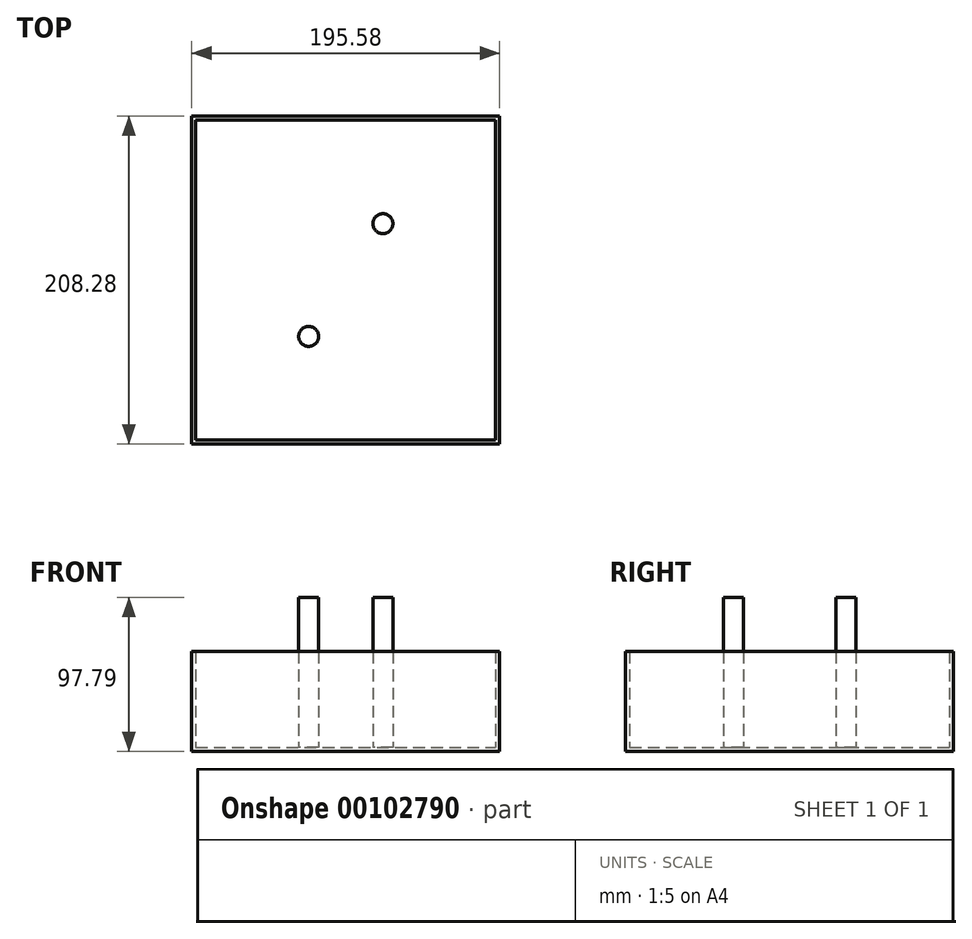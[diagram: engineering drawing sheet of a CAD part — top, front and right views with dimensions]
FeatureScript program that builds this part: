
annotation { "Feature Type Name" : "Feature", "Feature Type Description" : "" }
export const myFeature = defineFeature(function(context is Context, id is Id, definition is map)
    precondition{}
    {
        {
            var Q0;
            Q0=qCreatedBy(makeId("Top.planeOp"),FACE);
            var sketch = newSketch(context, id + "F0", { "sketchPlane" : qUnion([Q0])});
            skLineSegment(sketch, "E0", {"start": v(0, 0) * mm, "end": v(0, 104.14) * mm});
            skLineSegment(sketch, "E1", {"start": v(0, 104.14) * mm, "end": v(97.8, 104.14) * mm});
            skLineSegment(sketch, "E2", {"start": v(97.8, 104.14) * mm, "end": v(97.8, 0) * mm});
            skLineSegment(sketch, "E3.MirrorCS", {"start": v(0, 104.14) * mm, "end": v(-97.8, 104.14) * mm});
            skLineSegment(sketch, "E4.MirrorCS", {"start": v(97.8, -104.14) * mm, "end": v(97.79, 0) * mm});
            skLineSegment(sketch, "E5", {"start": v(-97.8, -104.14) * mm, "end": v(97.8, -104.14) * mm});
            skLineSegment(sketch, "E6", {"start": v(-97.8, -104.14) * mm, "end": v(-97.8, 104.14) * mm});
            skSolve(sketch);
        }
        {
            var Q0;
            Q0 = qSketchRegion(id + "F0", true);
            extrude(context, id + "F1", {"entities" : qUnion([Q0]), "depth" : 63.5 * mm});
        }
        {
            var Q0;
            Q0=makeQuery(id+"F1.opExtrude","CAP_FACE",FACE,{"disambiguationData":[OSD([sQuery(id+"F0.wireOp",EDGE,"E1"),sQuery(id+"F0.wireOp",EDGE,"E2"),sQuery(id+"F0.wireOp",EDGE,"8faf7771-bb4b-4e78-9b49-a767b9c531a00.MirrorCS"),sQuery(id+"F0.wireOp",EDGE,"E3.MirrorCS"),sQuery(id+"F0.wireOp",EDGE,"8fe53615-c728-4495-bf62-b4da586d37250.MirrorCS"),sQuery(id+"F0.wireOp",EDGE,"b9aa1892-de12-408e-bb1e-22edbf4f4b020.MirrorCS"),sQuery(id+"F0.wireOp",EDGE,"4fff83c6-06de-462e-9df9-fc56c3a055500.MirrorCS"),sQuery(id+"F0.wireOp",EDGE,"E4.MirrorCS")])],"isStart":false});
            shell(context, id + "F2", {"entities" : qUnion([Q0]), "thickness" : 2.54 * mm});
        }
        {
            var Q0;
            Q0=makeQuery(id+"F2.opShell","OFFSET_FACE",FACE,{"disambiguationData":[OSD([sQuery(id+"F0.wireOp",EDGE,"E1"),sQuery(id+"F0.wireOp",EDGE,"E2"),sQuery(id+"F0.wireOp",EDGE,"E3.MirrorCS"),sQuery(id+"F0.wireOp",EDGE,"E4.MirrorCS"),sQuery(id+"F0.wireOp",EDGE,"E5"),sQuery(id+"F0.wireOp",EDGE,"E6")])]});
            var sketch = newSketch(context, id + "F3", { "sketchPlane" : qUnion([Q0])});
            skCircle(sketch, "E7", {"center": v(-23.58, -35.83) * mm, "radius": 50.8 * mm});
            skCircle(sketch, "E8", {"center": v(23.58, 35.83) * mm, "radius": 34.3 * mm});
            skCircle(sketch, "E9", {"center": v(-23.58, -35.83) * mm, "radius": 6.35 * mm});
            skCircle(sketch, "E10", {"center": v(23.58, 35.83) * mm, "radius": 6.35 * mm});
            skSolve(sketch);
        }
        {
            var Q0;
            Q0=makeQuery(id+"F3.imprint","IMPRINT",FACE,{"disambiguationData":[TD([[makeQuery(id+"F3.imprint","IMPRINT",EDGE,{"derivedFrom":sQuery(id+"F3.wireOp",EDGE,"E10")}),1.0]])]});
            var Q1;
            Q1=makeQuery(id+"F3.imprint","IMPRINT",FACE,{"disambiguationData":[TD([[makeQuery(id+"F3.imprint","IMPRINT",EDGE,{"derivedFrom":sQuery(id+"F3.wireOp",EDGE,"E9")}),1.0]])]});
            extrude(context, id + "F4", {"entities" : qUnion([Q0, Q1]), "operationType" : NewBodyOperationType.ADD, "depth" : 95.25 * mm});
        }
    });
